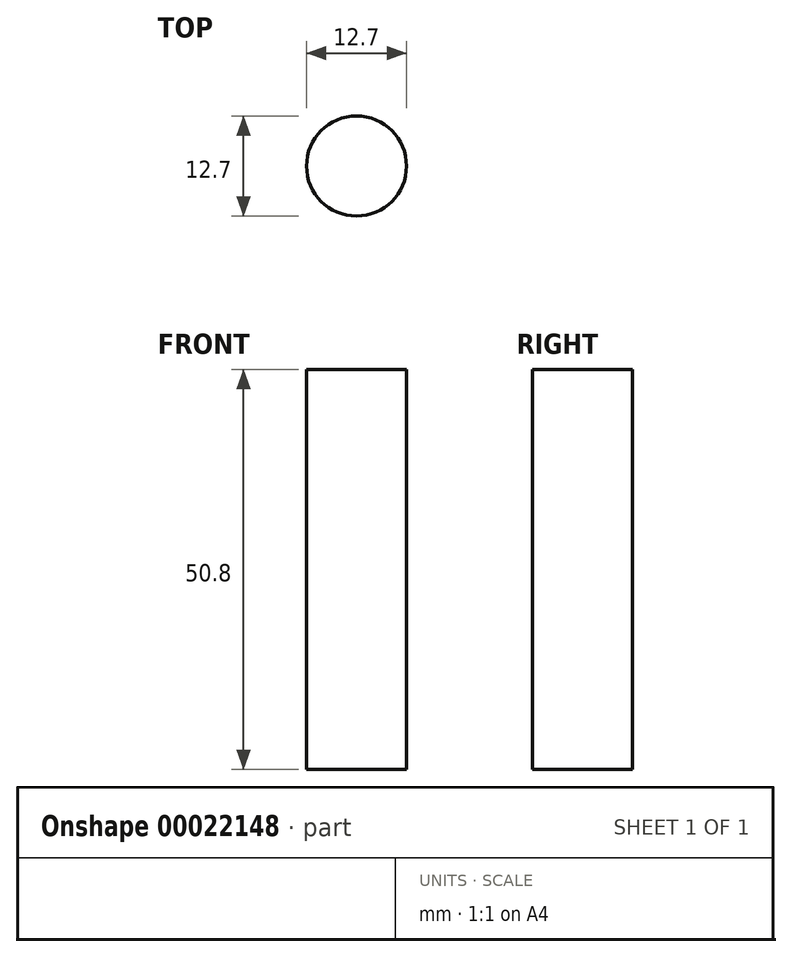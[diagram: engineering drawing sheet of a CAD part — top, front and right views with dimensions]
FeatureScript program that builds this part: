
annotation { "Feature Type Name" : "Feature", "Feature Type Description" : "" }
export const myFeature = defineFeature(function(context is Context, id is Id, definition is map)
    precondition{}
    {
        {
            var Q0;
            Q0=qCreatedBy(makeId("Top.planeOp"),FACE);
            var sketch = newSketch(context, id + "F0", { "sketchPlane" : qUnion([Q0])});
            skCircle(sketch, "E0", {"center": v(0, 0) * mm, "radius": 6.35 * mm});
            skSolve(sketch);
        }
        {
            var Q0;
            Q0=makeQuery(id+"F0.imprint","IMPRINT",FACE,{"disambiguationData":[TD([[makeQuery(id+"F0.imprint","IMPRINT",EDGE,{"derivedFrom":sQuery(id+"F0.wireOp",EDGE,"E0")}),1.0]])]});
            extrude(context, id + "F1", {"entities" : qUnion([Q0]), "endBound" : BoundingType.SYMMETRIC, "depth" : 50.8 * mm});
        }
    });
